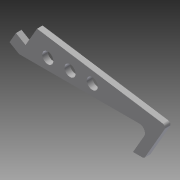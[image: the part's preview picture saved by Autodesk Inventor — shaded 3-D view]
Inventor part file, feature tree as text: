
AUTODESK INVENTOR PART (.ipt)
format: ipt  version: 2013 (Build 170138000, 138)  size: 117,760 bytes
history: native  units: in
note: dims shown in document units (in); Inventor stores cm internally (conversion verified against a paired STEP export)
features: extrude x3, fillet x3, sketch x3
ambient origin geometry x8: Origin, YZ Plane, XZ Plane, XY Plane, X Axis, Y Axis, Z Axis, Center Point
bodies: Solid1 (feature_tree)
feature tree (9):
  extrude  "Extrusion1"  Depth=1.25in
  extrude  "Extrusion2"  TaperAngle=60.0deg  [1 undecoded]
  fillet  "Fillet1"  [1 undecoded]
  fillet  "Fillet2"  Radius=0.5in
  extrude  "Extrusion3"  Depth=0.5in
  fillet  "Fillet4"  Radius=0.433in
  sketch  "Sketch1"  dims[d4=5.12in d7=1.25in]
  sketch  "Sketch2"  dims[d8=0.5in d9=60.0deg d10=60.0deg d11=0.5in]
  sketch  "Sketch3"  dims[d12=0.25in d13=0.0in d14=0.5in d15=0.433in d16=0.5774in d17=150.0deg d18=150.0deg d19=1.031in d20=0.25in d21=0.0in d22=0.125in d23=0.125in d26=0.5in d28=0.5in d30=0.5in d31=0.25in d32=0.0in d33=0.25in]
note: 2 required parameter values undecoded (feature->parameter linkage not recoverable at this tier; creation-order binding heuristic only, values carry confidence <= 0.55)
